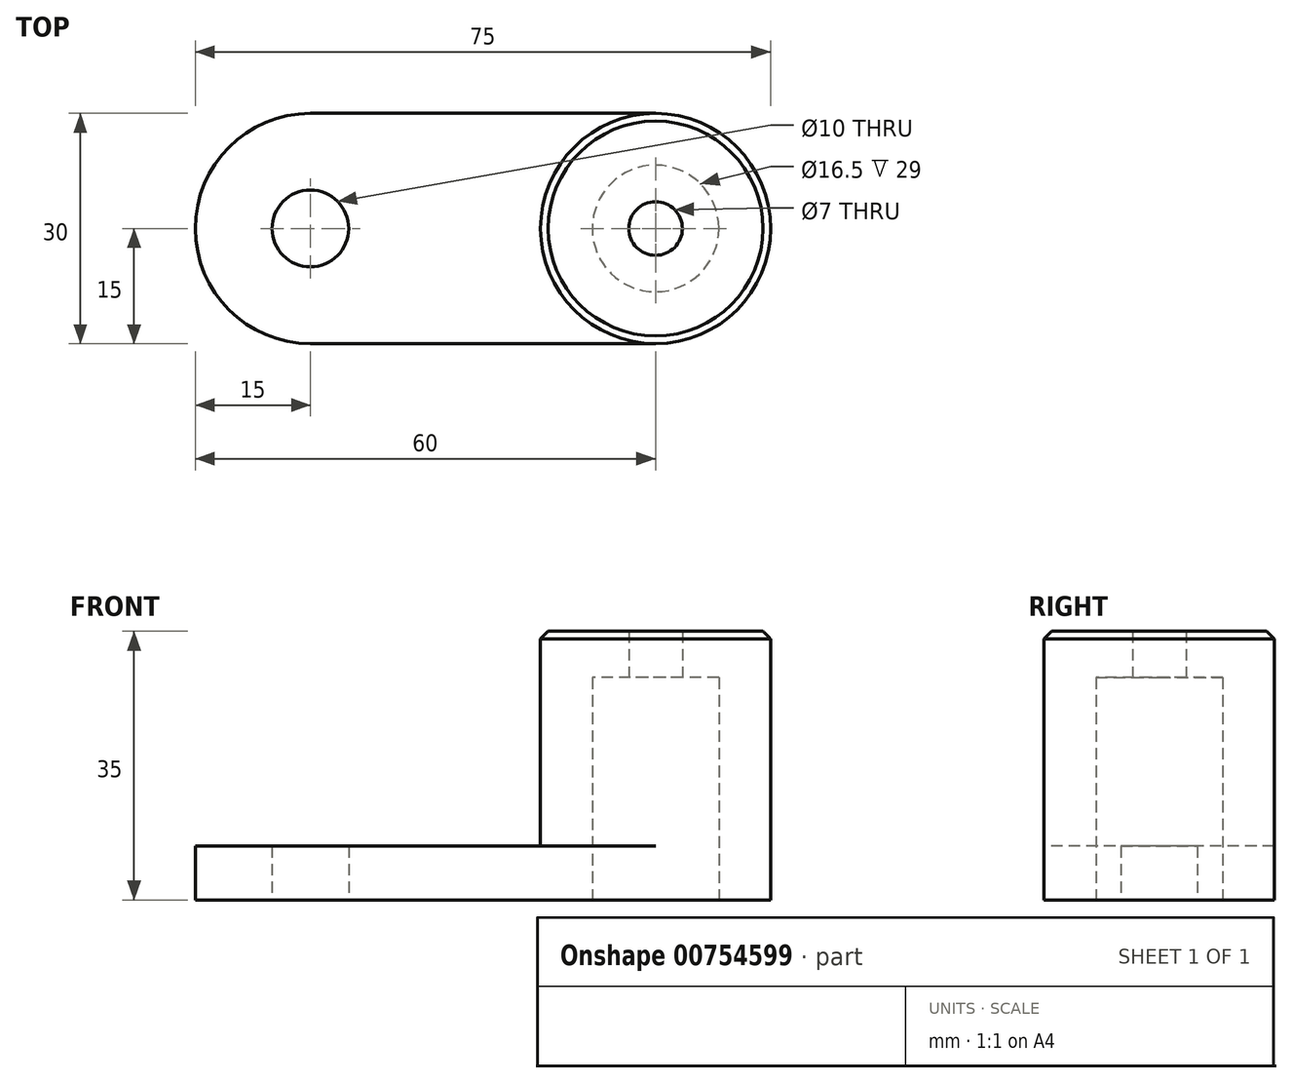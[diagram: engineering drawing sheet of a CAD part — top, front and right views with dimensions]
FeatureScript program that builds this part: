
annotation { "Feature Type Name" : "Feature", "Feature Type Description" : "" }
export const myFeature = defineFeature(function(context is Context, id is Id, definition is map)
    precondition{}
    {
        {
            var Q0;
            Q0=qCreatedBy(makeId("Top.planeOp"),FACE);
            var sketch = newSketch(context, id + "F0", { "sketchPlane" : qUnion([Q0])});
            skPoint(sketch, "E0.middle", {"position": v(0, 0) * mm});
            skCircle(sketch, "E1", {"center": v(-22.5, 0) * mm, "radius": 15 * mm});
            skCircle(sketch, "E2", {"center": v(22.5, 0) * mm, "radius": 15 * mm});
            skLineSegment(sketch, "E3", {"start": v(-22.5, 15) * mm, "end": v(-22.5, -15) * mm});
            skLineSegment(sketch, "E4", {"start": v(22.5, 15) * mm, "end": v(22.5, -15) * mm});
            skLineSegment(sketch, "E5.bottom", {"start": v(-22.5, 15) * mm, "end": v(22.5, 15) * mm});
            skLineSegment(sketch, "E5.top", {"start": v(-22.5, -15) * mm, "end": v(22.5, -15) * mm});
            skCircle(sketch, "E6", {"center": v(-22.5, 0) * mm, "radius": 5 * mm});
            skCircle(sketch, "E7", {"center": v(22.5, 0) * mm, "radius": 8.25 * mm});
            skSolve(sketch);
        }
        {
            var Q0;
            Q0 = qSketchRegion(id + "F0", true);
            extrude(context, id + "F1", {"entities" : qUnion([Q0]), "depth" : 7 * mm, "offsetDistance" : 25 * mm});
        }
        {
            var Q0;
            Q0=makeQuery(id+"F1.opExtrude","CAP_FACE",FACE,{"disambiguationData":[OSD([sQuery(id+"F0.wireOp",EDGE,"E1"),sQuery(id+"F0.wireOp",EDGE,"E2"),sQuery(id+"F0.wireOp",EDGE,"E5.bottom"),sQuery(id+"F0.wireOp",EDGE,"E5.top"),sQuery(id+"F0.wireOp",EDGE,"E6"),sQuery(id+"F0.wireOp",EDGE,"E7")])],"isStart":false});
            var sketch = newSketch(context, id + "F2", { "sketchPlane" : qUnion([Q0])});
            skCircle(sketch, "E8", {"center": v(22.5, 0) * mm, "radius": 15 * mm});
            skCircle(sketch, "E9", {"center": v(22.5, 0) * mm, "radius": 8.25 * mm});
            skSolve(sketch);
        }
        {
            var Q0;
            Q0 = qSketchRegion(id + "F2", true);
            extrude(context, id + "F3", {"entities" : qUnion([Q0]), "operationType" : NewBodyOperationType.ADD, "depth" : 22 * mm, "offsetDistance" : 25 * mm});
        }
        {
            var Q0;
            Q0=makeQuery(id+"F3.opExtrude","CAP_FACE",FACE,{"disambiguationData":[OSD([sQuery(id+"F2.wireOp",EDGE,"E8"),sQuery(id+"F2.wireOp",EDGE,"E9")])],"isStart":false});
            var sketch = newSketch(context, id + "F4", { "sketchPlane" : qUnion([Q0])});
            skCircle(sketch, "E10", {"center": v(22.5, 0) * mm, "radius": 3.5 * mm});
            skCircle(sketch, "E11", {"center": v(22.5, 0) * mm, "radius": 15 * mm});
            skSolve(sketch);
        }
        {
            var Q0;
            Q0 = qSketchRegion(id + "F4", true);
            extrude(context, id + "F5", {"entities" : qUnion([Q0]), "operationType" : NewBodyOperationType.ADD, "depth" : 6 * mm, "offsetDistance" : 25 * mm});
        }
        {
            var Q0;
            Q0=makeQuery(id+"F5.opExtrude","CAP_EDGE",EDGE,{"disambiguationData":[OSD([sQuery(id+"F4.wireOp",EDGE,"E11")])],"isStart":false});
            chamfer(context, id + "F6", {"entities" : qUnion([Q0]), "chamferType" : ChamferType.OFFSET_ANGLE, "width" : 1 * mm, "oppositeDirection" : false, "angle" : 45 * degree, "tangentPropagation" : true});
        }
    });
